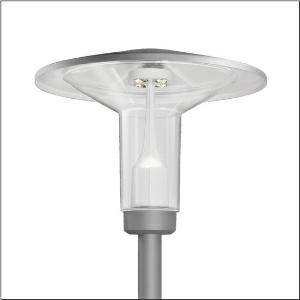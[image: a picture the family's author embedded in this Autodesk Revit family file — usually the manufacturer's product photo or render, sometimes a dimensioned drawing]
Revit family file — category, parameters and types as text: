
# Revit family: laterne_iq___st1_2a_5xa5255ef14h_6af0
name_source: partatom
category: Lighting Fixtures
units: mm (PartAtom-declared; Revit-internal decimal feet)

## family parameters
Cut with Voids When Loaded = No
Host = Face
Light Source = No
Part Type = Normal
Room Calculation Point = No
Round Connector Dimension = Use Diameter
Shared = No

## types (1)
- --- (1 x LED, 1540 lm, 10.5 W, 3000K)
    Apparent Load = 11 VA
    CIE Flux Codes = 25 63 94 98 100
    Color Rendering = 70
    Color Temperature = 3000K
    Default Elevation = 1800 mm
    Description = Lantern iQ, mast luminaire, Module 540 iQ-SR, primary light control with 3 zone facetted reflector, of plastic, silver coated, highly specular, structured, primary optical cover: cover, of PMMA, transparent, light distribution: ST1.2a, light emission: direct distribution, primary light characteristic: asymmetric, installation type: post-top, LED, High Power LED, rated luminous flux: 1.540lm, luminous efficacy: 147lm/W, light colour: 730, colour temperature: 3000K, control gear: ECG iQ, control: Auto-Match, Temp-Guard, Lumen-Switch, Night-Set, Smart-Wire, Light-Fading, Desk-Remote (wireless, voltage-free reading and setting of iQ features in the workshop via application-optimized NFC function/RFID function), optimised constant luminous flux control (CLO 2.0), Street-Remote, presetting dimming logarithmic, with terminal, 6-pole, max. 2.5mm², mains connection: 230..240V, AC, 50/60Hz, start of lifetime: 11W, end of service life: 11W, reduction: 5W, luminaire housing, upper part, of glass-fibre reinforced polyester, coated, Siteco® metallic grey (DB 702S), diameter: 750mm, height: 583mm, spigot size: d x l = 76 x 70mm (post-top) | with reducer (optional accessory) 60 x 70mm, post-top mast mounting element, of diecast aluminium, coated, Siteco® metallic grey (DB 702S), Module 540 iQ-SR, traffic white (RAL 9016), equipment: standard, protection rating (complete): IP65, insulation class (complete): insulation class II (safety insulation), certification: CE, ENEC, VDE, packaging unit: 1 piece

Light Distribution: ST1.2a
    Height = 583 mm
    Lamp = 1 x LED
    Lamp Light Flux = 1540 lm
    Lamp Power = 10.5 W
    Lamp count = 1
    Length = 750 mm
    Luminous efficacy = 147 lm/W
    Manufacturer = Siteco
    ModVariant = No
    Model = 5XA5255EF14H
    Number of Poles = 1
    OnlyDefault = Yes
    Power Factor = 1
    Product Name = Laterne iQ | ST1.2a
    Product group = mast luminaire | pylon top
    ProductGroupID = 6100
    Protection Class = Protection class II
    Protection Degree = IP 65
    RLX_Detail_Level = 1
    RLX_Emergency_Light_Flux = 0 lm
    RLX_Emergency_Type = 0
    RLX_Emergency_Type_DB = No
    RlxData = <blob elided: 103337 chars, md5=a89d5cfd>
    Socket = socket
    Standby Power = 0 W
    System Light Flux = 1540 lm
    System Power = 11 W
    Type Comments = factory setting: luminous flux: 100 % | dim-lin: 254 | 419 mA
    Type Image = l_1006050.jpg
    URL = http://relux.com
    VarID = @adj_092959
    Voltage = 0 V
    Weight = 0.00 kg
    Width = 0 mm  [stored 0 ft]

note: [stored X ft] marks values corroborated as IEEE doubles in the binary element streams (Revit-internal decimal feet)

## geometry (parser evidence)
native form markers: Blend x4, Sweep x9
no freeform markers — native parametric forms only
